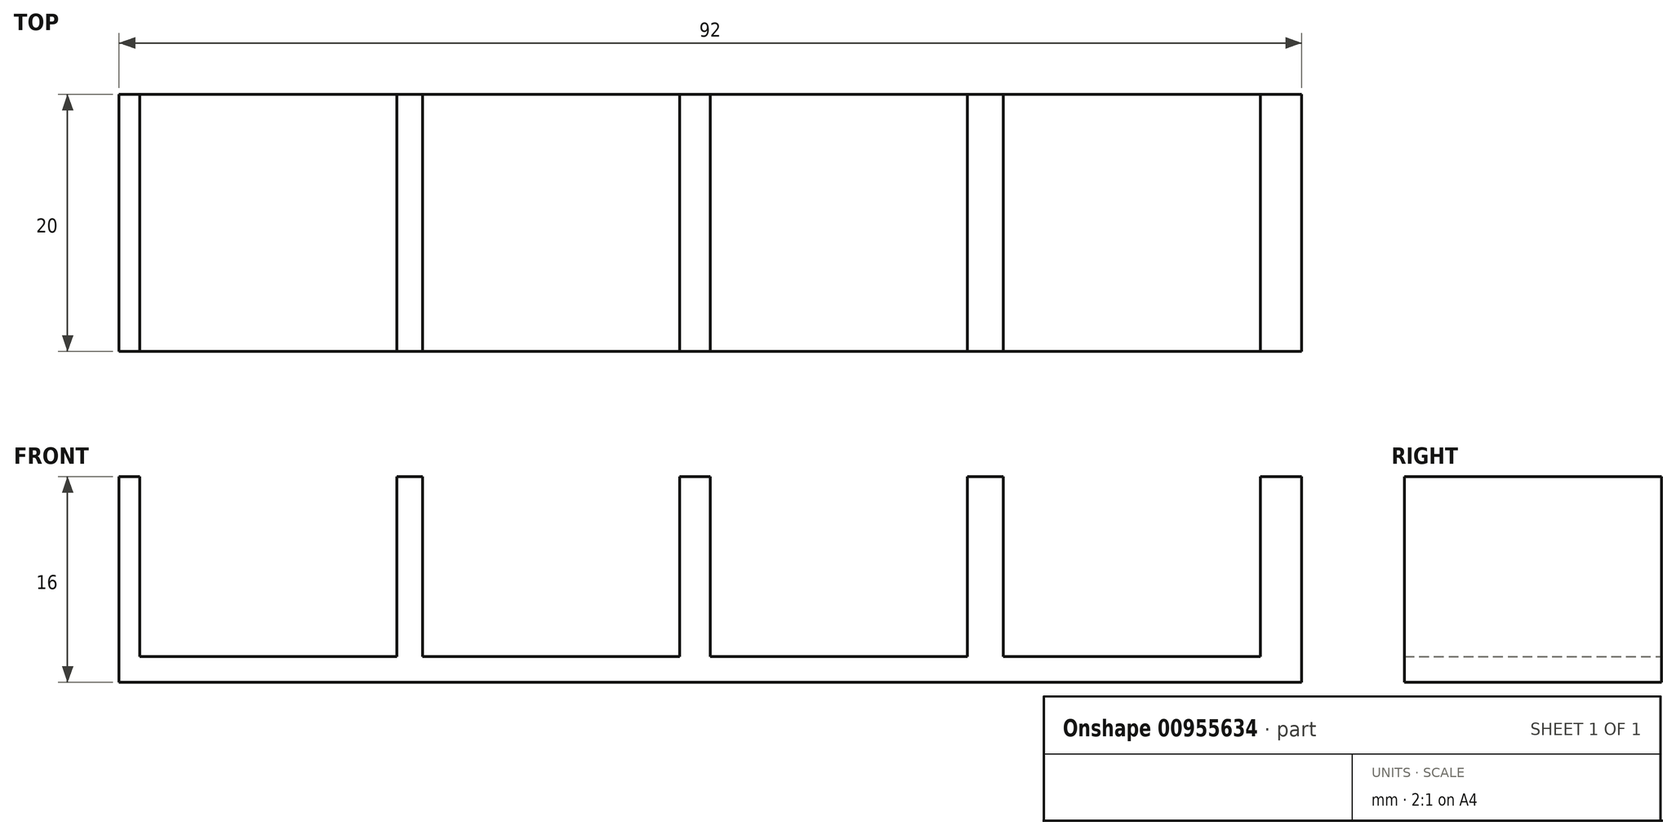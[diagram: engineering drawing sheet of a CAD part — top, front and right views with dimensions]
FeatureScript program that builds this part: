
annotation { "Feature Type Name" : "Feature", "Feature Type Description" : "" }
export const myFeature = defineFeature(function(context is Context, id is Id, definition is map)
    precondition{}
    {
        {
            var Q0;
            Q0=qCreatedBy(makeId("Top.planeOp"),FACE);
            var sketch = newSketch(context, id + "F0", { "sketchPlane" : qUnion([Q0])});
            skLineSegment(sketch, "E0.bottom", {"start": v(0, 0) * mm, "end": v(92, 0) * mm});
            skLineSegment(sketch, "E0.top", {"start": v(0, -20) * mm, "end": v(92, -20) * mm});
            skLineSegment(sketch, "E0.left", {"start": v(0, 0) * mm, "end": v(0, -20) * mm});
            skLineSegment(sketch, "E0.right", {"start": v(92, 0) * mm, "end": v(92, -20) * mm});
            skSolve(sketch);
        }
        {
            var Q0;
            Q0=makeQuery(id+"F0.imprint","IMPRINT",FACE,{"disambiguationData":[TD([[makeQuery(id+"F0.imprint","IMPRINT",EDGE,{"derivedFrom":sQuery(id+"F0.wireOp",EDGE,"E0.bottom")}),-1.0]])]});
            extrude(context, id + "F1", {"entities" : qUnion([Q0]), "depth" : 2 * mm, "offsetDistance" : 25 * mm});
        }
        {
            var Q0;
            Q0=makeQuery(id+"F1.opExtrude","CAP_FACE",FACE,{"disambiguationData":[OSD([sQuery(id+"F0.wireOp",EDGE,"E0.bottom"),sQuery(id+"F0.wireOp",EDGE,"E0.top"),sQuery(id+"F0.wireOp",EDGE,"E0.left"),sQuery(id+"F0.wireOp",EDGE,"E0.right")])],"isStart":false});
            var sketch = newSketch(context, id + "F2", { "sketchPlane" : qUnion([Q0])});
            skLineSegment(sketch, "E1", {"start": v(0, -20) * mm, "end": v(0, -20) * mm});
            skLineSegment(sketch, "E2", {"start": v(0, -20) * mm, "end": v(0, 0) * mm});
            skLineSegment(sketch, "E3.0", {"start": v(1.6, -20) * mm, "end": v(1.6, 0) * mm});
            skLineSegment(sketch, "E4.0", {"start": v(21.6, -20) * mm, "end": v(21.6, 0) * mm});
            skLineSegment(sketch, "E5.0", {"start": v(23.6, -20) * mm, "end": v(23.6, 0) * mm});
            skLineSegment(sketch, "E6.0", {"start": v(43.6, -20) * mm, "end": v(43.6, 0) * mm});
            skLineSegment(sketch, "E7.0", {"start": v(46, -20) * mm, "end": v(46, 0) * mm});
            skLineSegment(sketch, "E8.0", {"start": v(66, -20) * mm, "end": v(66, 0) * mm});
            skLineSegment(sketch, "E9.0", {"start": v(68.8, -20) * mm, "end": v(68.8, 0) * mm});
            skLineSegment(sketch, "E10.0", {"start": v(88.8, -20) * mm, "end": v(88.8, 0) * mm});
            skLineSegment(sketch, "E11.0", {"start": v(92, -20) * mm, "end": v(92, 0) * mm});
            skSolve(sketch);
        }
        {
            var Q0;
            {var subQ0=sQuery(id+"F2.wireOp",EDGE,"E2");Q0=makeQuery(id+"F2.imprint","IMPRINT",FACE,{"disambiguationData":[TD([[makeQuery(id+"F2.imprint","IMPRINT",EDGE,{"derivedFrom":subQ0}),1.0]])]});}
            var Q1;
            {var subQ0=sQuery(id+"F2.wireOp",EDGE,"E4.0");Q1=makeQuery(id+"F2.imprint","IMPRINT",FACE,{"disambiguationData":[TD([[makeQuery(id+"F2.imprint","IMPRINT",EDGE,{"derivedFrom":subQ0}),-1.0]])]});}
            var Q2;
            {var subQ0=sQuery(id+"F2.wireOp",EDGE,"E6.0");Q2=makeQuery(id+"F2.imprint","IMPRINT",FACE,{"disambiguationData":[TD([[makeQuery(id+"F2.imprint","IMPRINT",EDGE,{"derivedFrom":subQ0}),-1.0]])]});}
            var Q3;
            {var subQ0=sQuery(id+"F2.wireOp",EDGE,"E8.0");Q3=makeQuery(id+"F2.imprint","IMPRINT",FACE,{"disambiguationData":[TD([[makeQuery(id+"F2.imprint","IMPRINT",EDGE,{"derivedFrom":subQ0}),-1.0]])]});}
            var Q4;
            {var subQ0=sQuery(id+"F2.wireOp",EDGE,"E10.0");Q4=makeQuery(id+"F2.imprint","IMPRINT",FACE,{"disambiguationData":[TD([[makeQuery(id+"F2.imprint","IMPRINT",EDGE,{"derivedFrom":subQ0}),-1.0]])]});}
            extrude(context, id + "F3", {"entities" : qUnion([Q0, Q1, Q2, Q3, Q4]), "operationType" : NewBodyOperationType.ADD, "depth" : 14 * mm, "offsetDistance" : 25 * mm});
        }
    });
